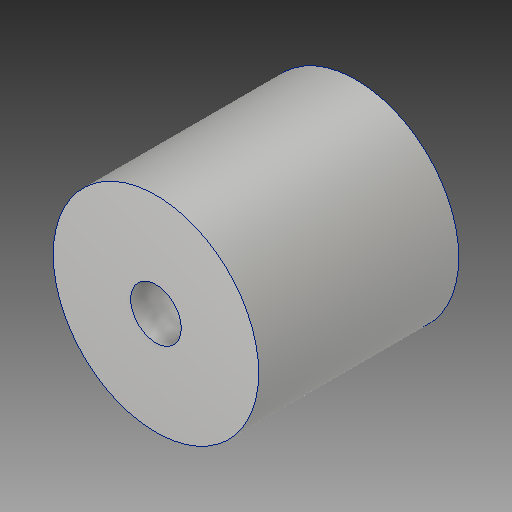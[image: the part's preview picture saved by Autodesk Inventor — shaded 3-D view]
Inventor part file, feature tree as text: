
AUTODESK INVENTOR PART (.ipt)
format: ipt  version: 2017 (Build 210142000, 142)  size: 116,224 bytes
history: native  units: in
note: dims shown in document units (in); Inventor stores cm internally (conversion verified against a paired STEP export)
features: chamfer x1
ambient origin geometry x8: Origin, YZ Plane, XZ Plane, XY Plane, X Axis, Y Axis, Z Axis, Center Point
bodies: Solid1 (feature_tree)
feature tree (1):
  chamfer  "Chamfer2"  [1 undecoded]
note: 1 required parameter value undecoded (feature->parameter linkage not recoverable at this tier; creation-order binding heuristic only, values carry confidence <= 0.55)
